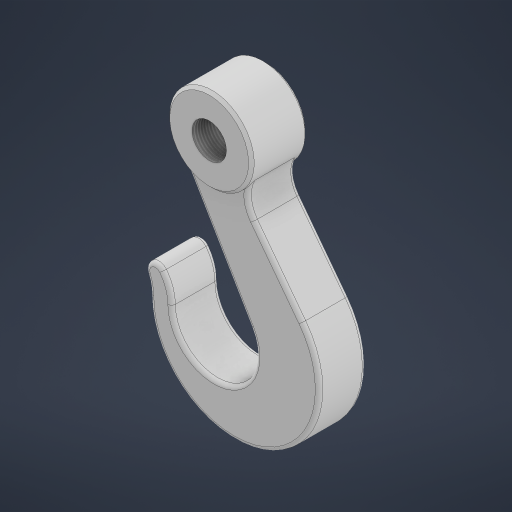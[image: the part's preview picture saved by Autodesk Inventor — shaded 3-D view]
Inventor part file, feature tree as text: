
AUTODESK INVENTOR PART (.ipt)
format: ipt  version: 2023 (Build 270158000, 158)  size: 286,720 bytes
history: native  units: mm
features: sketch x4, emboss x2, extrude x1, hole x1, fillet x1, chamfer x1
ambient origin geometry x8: Origin, YZ Plane, XZ Plane, XY Plane, X Axis, Y Axis, Z Axis, Center Point
bodies: Solid1 (feature_tree)
feature tree (10):
  extrude  "Extrusion1"  Depth=180.0mm
  emboss  "Emboss1"
  emboss  "Emboss2"
  hole  "Hole2"  [1 undecoded]
  fillet  "Fillet1"  Radius=178.0mm
  chamfer  "Chamfer1"  Distance=45.0mm
  sketch  "Sketch2"  dims[d9=90.0mm d10=180.0mm]
  sketch  "Sketch5"  dims[d11=22.0mm d12=90.0mm d13=178.0mm]
  sketch  "Sketch6"  dims[d14=32.0mm]
  sketch  "Sketch7"  dims[d15=45.0mm d16=45.0mm d17=10.0mm d18=50.0mm d19=0.0mm d29=90.0mm d30=5.0mm d31=0.0mm d32=90.0mm d33=5.0mm d34=0.0mm d35=36.752404mm d36=80.0mm d37=20.0mm d38=2.0mm d39=90.0deg d40=8.0mm d41=20.594885mm d42=4.0mm d43=3.0mm d44=3.0mm d45=45.0deg d46=0.25mm d47=0.375mm d48=14.3117mm d49=0.75mm d50=20.594885mm d51=0.0625mm d52=0.75mm d53=0.375mm]
note: 1 required parameter value undecoded (feature->parameter linkage not recoverable at this tier; creation-order binding heuristic only, values carry confidence <= 0.55)
